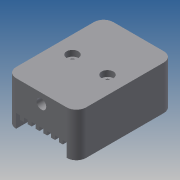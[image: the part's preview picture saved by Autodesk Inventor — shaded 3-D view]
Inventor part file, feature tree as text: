
AUTODESK INVENTOR PART (.ipt)
format: ipt  version: 2013 (Build 170138000, 138)  size: 200,192 bytes
history: native  units: mm
features: extrude x8, sketch x8, fillet x3, projected_geometry x2, pattern_linear x1, mirror x1
ambient origin geometry x8: Origin, YZ Plane, XZ Plane, XY Plane, X Axis, Y Axis, Z Axis, Center Point
bodies: Solid1 (feature_tree)
feature tree (23):
  extrude  "Extrusion1"  Depth=40.0mm
  extrude  "Extrusion3"  Depth=12.5mm TaperAngle=0.0deg
  extrude  "Extrusion4"  Depth=21.0mm
  extrude  "Extrusion5"  Depth=2.0mm
  pattern_linear  "Rectangular Pattern1"  Count1=7 Spacing1=4.0mm
  extrude  "Extrusion6"  Depth=5.0mm
  extrude  "Extrusion7"  Depth=5.0mm TaperAngle=0.0deg
  fillet  "Fillet3"  Radius=5.0mm
  extrude  "Extrusion8"  Depth=5.0mm
  extrude  "Extrusion9"  Depth=6.0mm
  mirror  "Mirror1"
  fillet  "Fillet1"  Radius=9.0mm
  fillet  "Fillet2"  Radius=3.0mm
  sketch  "Sketch1"  dims[d0=26.0mm d1=40.0mm]
  sketch  "Sketch3"  dims[d2=5.0mm d3=12.5mm d4=0.0mm]
  projected_geometry  "Projected Loop1"
  sketch  "Sketch4"  dims[d9=5.0mm d10=0.0mm d11=21.0mm]
  sketch  "Sketch5"  dims[d13=1.0mm d14=0.0mm d15=2.0mm]
  sketch  "Sketch6"  dims[d17=1.0mm d18=0.0mm d19=70.0mm d21=4.0mm]
  sketch  "Sketch7"  dims[d22=12.5mm d23=5.0mm]
  projected_geometry  "Projected Loop2"
  sketch  "Sketch8"  dims[d24=1.0mm d25=0.0mm d26=5.0mm d27=0.0mm d28=5.0mm]
  sketch  "Sketch9"  dims[d29=5.0mm d30=5.0mm d31=6.0mm d34=9.0mm d35=3.0mm d36=0.0mm d37=3.5mm d39=3.0mm d40=0.0mm]
